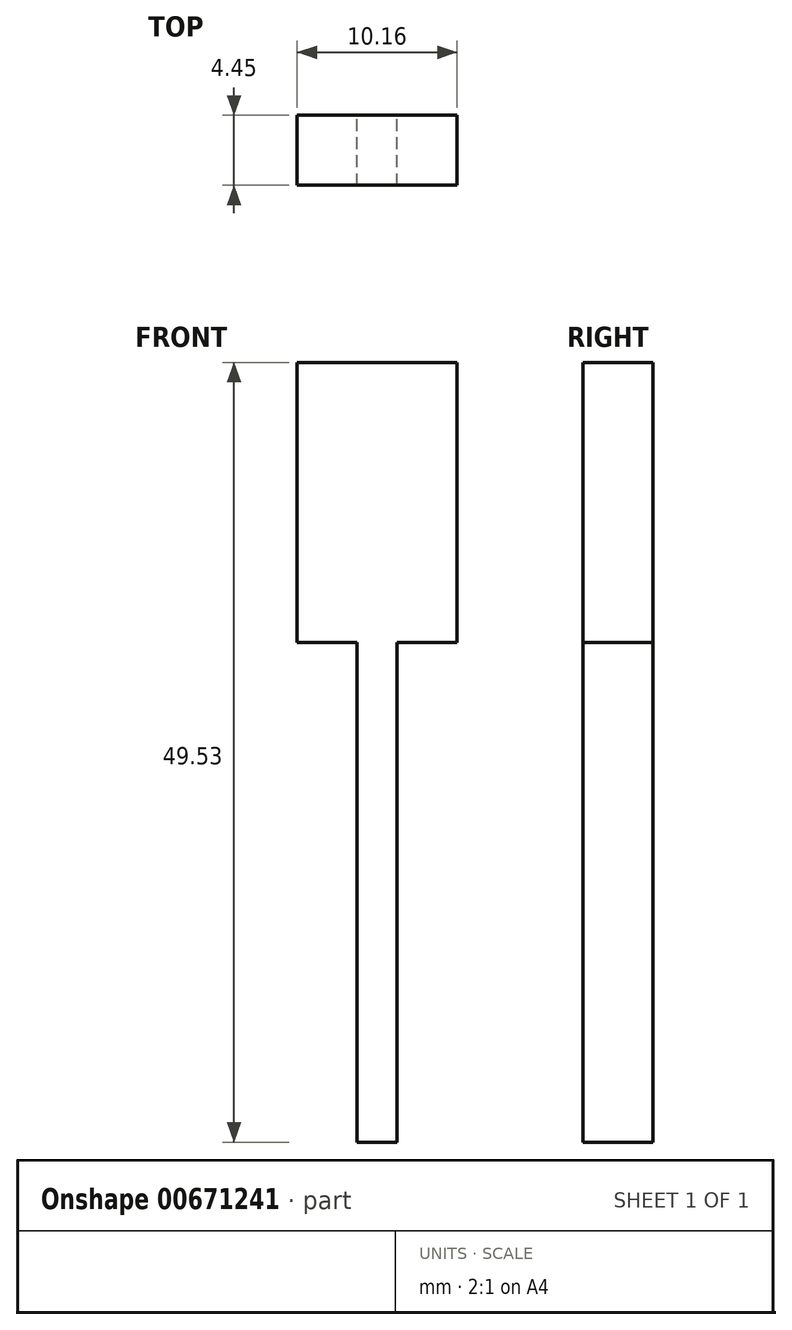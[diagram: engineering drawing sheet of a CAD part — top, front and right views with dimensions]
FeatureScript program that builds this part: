
annotation { "Feature Type Name" : "Feature", "Feature Type Description" : "" }
export const myFeature = defineFeature(function(context is Context, id is Id, definition is map)
    precondition{}
    {
        {
            var Q0;
            Q0=qCreatedBy(makeId("Front.planeOp"),FACE);
            var sketch = newSketch(context, id + "F0", { "sketchPlane" : qUnion([Q0])});
            skLineSegment(sketch, "E0.bottom", {"start": v(-11.85, -4.97) * mm, "end": v(-1.7, -4.97) * mm});
            skLineSegment(sketch, "E0.top", {"start": v(-11.85, -22.75) * mm, "end": v(-1.7, -22.75) * mm});
            skLineSegment(sketch, "E0.left", {"start": v(-11.85, -4.97) * mm, "end": v(-11.85, -22.75) * mm});
            skLineSegment(sketch, "E0.right", {"start": v(-1.7, -4.97) * mm, "end": v(-1.7, -22.75) * mm});
            skLineSegment(sketch, "E1.bottom", {"start": v(-8.04, -22.75) * mm, "end": v(-5.5, -22.75) * mm});
            skLineSegment(sketch, "E1.top", {"start": v(-8.04, -54.5) * mm, "end": v(-5.5, -54.5) * mm});
            skLineSegment(sketch, "E1.left", {"start": v(-8.04, -22.75) * mm, "end": v(-8.04, -54.5) * mm});
            skLineSegment(sketch, "E1.right", {"start": v(-5.5, -22.75) * mm, "end": v(-5.5, -54.5) * mm});
            skSolve(sketch);
        }
        {
            var Q0;
            Q0 = qSketchRegion(id + "F0", true);
            extrude(context, id + "F1", {"entities" : qUnion([Q0]), "depth" : 4.44 * mm, "offsetDistance" : 25.4 * mm});
        }
    });
